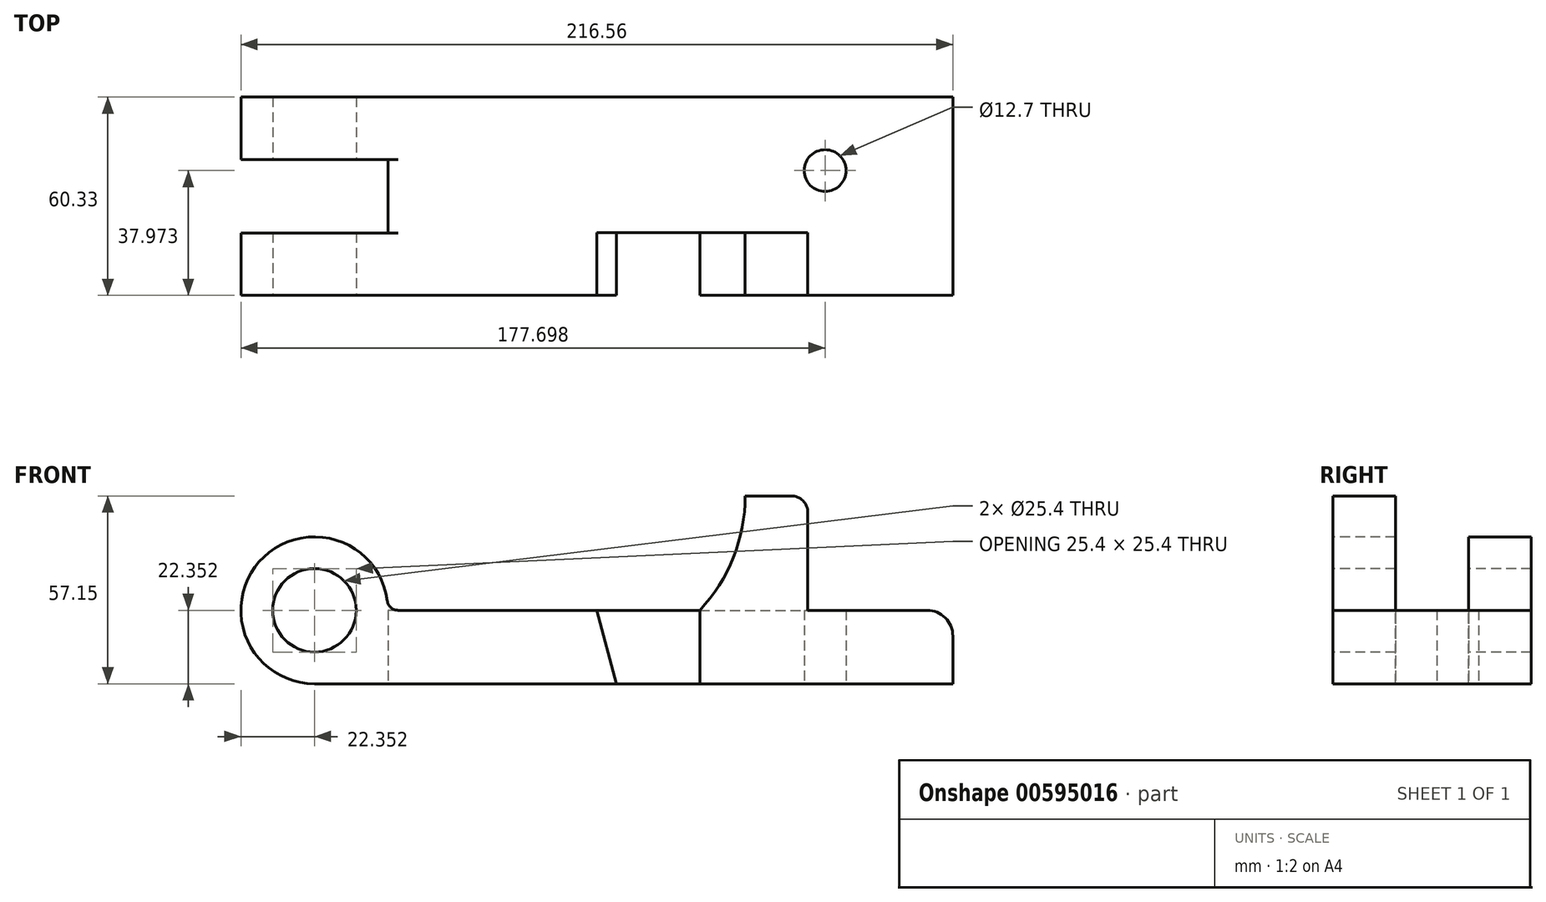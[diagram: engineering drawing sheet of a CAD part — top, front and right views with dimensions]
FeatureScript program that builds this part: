
annotation { "Feature Type Name" : "Feature", "Feature Type Description" : "" }
export const myFeature = defineFeature(function(context is Context, id is Id, definition is map)
    precondition{}
    {
        {
            var Q0;
            Q0=qCreatedBy(makeId("Front.planeOp"),FACE);
            var sketch = newSketch(context, id + "F0", { "sketchPlane" : qUnion([Q0])});
            skLineSegment(sketch, "E0", {"start": v(-102.09, 0) * mm, "end": v(92.12, 0) * mm});
            skLineSegment(sketch, "E1", {"start": v(92.12, 0) * mm, "end": v(92.12, 14.48) * mm});
            skLineSegment(sketch, "E2", {"start": v(84.25, 22.35) * mm, "end": v(48, 22.35) * mm});
            skLineSegment(sketch, "E3", {"start": v(48, 22.35) * mm, "end": v(48, 52.07) * mm});
            skLineSegment(sketch, "E4", {"start": v(42.92, 57.15) * mm, "end": v(28.95, 57.15) * mm});
            skLineSegment(sketch, "E5", {"start": v(15.16, 22.35) * mm, "end": v(-79.74, 22.35) * mm});
            skArc(sketch, "E6", {"start": v(-79.74, 22.35) * mm, "mid": v(-117.9, 38.16) * mm, "end": v(-102.09, 0) * mm});
            skCircle(sketch, "E7", {"center": v(-102.09, 22.35) * mm, "radius": 12.7 * mm});
            skArc(sketch, "E8.filletArc", {"start": v(92.12, 14.48) * mm, "mid": v(89.81, 20.05) * mm, "end": v(84.25, 22.35) * mm});
            skArc(sketch, "E9.filletArc", {"start": v(48, 52.07) * mm, "mid": v(46.51, 55.66) * mm, "end": v(42.92, 57.15) * mm});
            skArc(sketch, "E10", {"start": v(15.16, 22.35) * mm, "mid": v(25.38, 38.43) * mm, "end": v(28.95, 57.15) * mm});
            skSolve(sketch);
        }
        {
            var Q0;
            Q0=makeQuery(id+"F0.imprint","IMPRINT",FACE,{"disambiguationData":[TD([[makeQuery(id+"F0.imprint","IMPRINT",EDGE,{"derivedFrom":sQuery(id+"F0.wireOp",EDGE,"E0")}),1.0]])]});
            extrude(context, id + "F1", {"entities" : qUnion([Q0]), "oppositeDirection" : true, "depth" : 60.32 * mm});
        }
        {
            var Q0;
            Q0=makeQuery(id+"F1.opExtrude","SWEPT_FACE",FACE,{"disambiguationData":[OSD([sQuery(id+"F0.wireOp",EDGE,"E5")])]});
            cPlane(context, id + "F2", {"entities" : qUnion([Q0]), "cplaneType" : CPlaneType.OFFSET, "offset" : 0 * mm, "width" : 152.4 * mm, "height" : 152.4 * mm});
        }
        {
            var Q0;
            Q0=qCreatedBy(id+"F2.planeOp",FACE);
            var sketch = newSketch(context, id + "F3", { "sketchPlane" : qUnion([Q0])});
            skLineSegment(sketch, "E11.0", {"start": v(15.16, 60.33) * mm, "end": v(15.16, 19.05) * mm});
            skLineSegment(sketch, "E12.0", {"start": v(48, 60.33) * mm, "end": v(48, 19.05) * mm});
            skLineSegment(sketch, "E13", {"start": v(15.16, 60.33) * mm, "end": v(48, 60.33) * mm});
            skLineSegment(sketch, "E14", {"start": v(15.16, 19.05) * mm, "end": v(48, 19.05) * mm});
            skSolve(sketch);
        }
        {
            var Q0;
            Q0=qCreatedBy(makeId("Front.planeOp"),FACE);
            var sketch = newSketch(context, id + "F4", { "sketchPlane" : qUnion([Q0])});
            skLineSegment(sketch, "E15", {"start": v(15.16, 22.35) * mm, "end": v(15.16, 0) * mm});
            skLineSegment(sketch, "E16", {"start": v(15.16, 0) * mm, "end": v(-10.24, 0) * mm});
            skLineSegment(sketch, "E17", {"start": v(-10.24, 0) * mm, "end": v(-16.24, 22.35) * mm});
            skLineSegment(sketch, "E18", {"start": v(-16.24, 22.35) * mm, "end": v(15.16, 22.35) * mm});
            skCircle(sketch, "E19.0", {"center": v(-102.09, 22.35) * mm, "radius": 12.7 * mm, "construction": true});
            skSolve(sketch);
        }
        {
            var Q0;
            Q0=qCreatedBy(id+"F2.planeOp",FACE);
            var sketch = newSketch(context, id + "F5", { "sketchPlane" : qUnion([Q0])});
            skLineSegment(sketch, "E20.0", {"start": v(-79.74, 41.33) * mm, "end": v(-79.74, 19) * mm});
            skCircle(sketch, "E21", {"center": v(53.26, 37.97) * mm, "radius": 6.35 * mm});
            skLineSegment(sketch, "E22", {"start": v(-130.19, 41.33) * mm, "end": v(-130.19, 19) * mm});
            skLineSegment(sketch, "E23", {"start": v(-130.19, 41.33) * mm, "end": v(-79.74, 41.33) * mm});
            skLineSegment(sketch, "E24", {"start": v(-130.19, 19) * mm, "end": v(-79.74, 19) * mm});
            skSolve(sketch);
        }
        {
            var Q0;
            Q0=qSketchRegion(id+"F3",true);
            extrude(context, id + "F6", {"entities" : qUnion([Q0]), "operationType" : NewBodyOperationType.REMOVE, "endBound" : BoundingType.UP_TO_NEXT, "depth" : 25.4 * mm, "offsetDistance" : 25.4 * mm});
        }
        {
            var Q0;
            Q0=qSketchRegion(id+"F4",true);
            extrude(context, id + "F7", {"entities" : qUnion([Q0]), "operationType" : NewBodyOperationType.REMOVE, "oppositeDirection" : true, "depth" : 19.05 * mm});
        }
        {
            var Q0;
            Q0=qSketchRegion(id+"F5",true);
            extrude(context, id + "F8", {"entities" : qUnion([Q0]), "operationType" : NewBodyOperationType.REMOVE, "endBound" : BoundingType.SYMMETRIC, "depth" : 95 * mm, "offsetDistance" : 25.4 * mm});
        }
        {
            var Q0;
            {var subQ0=sQuery(id+"F0.wireOp",EDGE,"E6");var subQ1=makeQuery(id+"F1.opExtrude","SWEPT_FACE",FACE,{"disambiguationData":[OSD([subQ0])]});var subQ2=sQuery(id+"F0.wireOp",EDGE,"E5");var subQ3=makeQuery(id+"F1.opExtrude","SWEPT_FACE",FACE,{"disambiguationData":[OSD([subQ2])]});var subQ4=sQuery(id+"F0.wireOp",EDGE,"E2");var subQ5=makeQuery(id+"F1.opExtrude","SWEPT_FACE",FACE,{"disambiguationData":[OSD([subQ4])]});var subQ6=makeQuery(id+"F6.opExtrude","CAP_FACE",FACE,{"disambiguationData":[OSD([sQuery(id+"F3.wireOp",EDGE,"E11.0"),sQuery(id+"F3.wireOp",EDGE,"E12.0"),sQuery(id+"F3.wireOp",EDGE,"E13"),sQuery(id+"F3.wireOp",EDGE,"E14")])],"isStart":true});Q0=makeQuery(id+"F8.boolean.opBoolean","SPLIT",EDGE,{"disambiguationData":[topologyDisambiguationEdgeConnected([subQ5,subQ3,subQ1,subQ6]),TD([makeQuery(id+"F8.opExtrude","SWEPT_FACE",FACE,{"disambiguationData":[OSD([sQuery(id+"F5.wireOp",EDGE,"E24")])]})])],"derivedFrom":makeQuery(id+"F1.opExtrude","SWEPT_EDGE",EDGE,{"disambiguationData":[OSD([subQ2,subQ0])]})});}
            var Q1;
            {var subQ0=sQuery(id+"F0.wireOp",EDGE,"E6");var subQ1=makeQuery(id+"F1.opExtrude","SWEPT_FACE",FACE,{"disambiguationData":[OSD([subQ0])]});var subQ2=sQuery(id+"F0.wireOp",EDGE,"E2");var subQ3=makeQuery(id+"F1.opExtrude","SWEPT_FACE",FACE,{"disambiguationData":[OSD([subQ2])]});var subQ4=makeQuery(id+"F6.opExtrude","CAP_FACE",FACE,{"disambiguationData":[OSD([sQuery(id+"F3.wireOp",EDGE,"E11.0"),sQuery(id+"F3.wireOp",EDGE,"E12.0"),sQuery(id+"F3.wireOp",EDGE,"E13"),sQuery(id+"F3.wireOp",EDGE,"E14")])],"isStart":true});var subQ5=sQuery(id+"F0.wireOp",EDGE,"E5");var subQ6=makeQuery(id+"F1.opExtrude","SWEPT_FACE",FACE,{"disambiguationData":[OSD([subQ5])]});Q1=makeQuery(id+"F8.boolean.opBoolean","SPLIT",EDGE,{"disambiguationData":[topologyDisambiguationEdgeConnected([subQ3,subQ6,subQ1,subQ4]),TD([makeQuery(id+"F8.opExtrude","SWEPT_FACE",FACE,{"disambiguationData":[OSD([sQuery(id+"F5.wireOp",EDGE,"E23")])]})])],"derivedFrom":makeQuery(id+"F1.opExtrude","SWEPT_EDGE",EDGE,{"disambiguationData":[OSD([subQ5,subQ0])]})});}
            fillet(context, id + "F9", {"entities" : qUnion([Q0, Q1]), "radius" : 3.3 * mm, "tangentPropagation" : true, "allowEdgeOverflow" : false});
        }
    });
